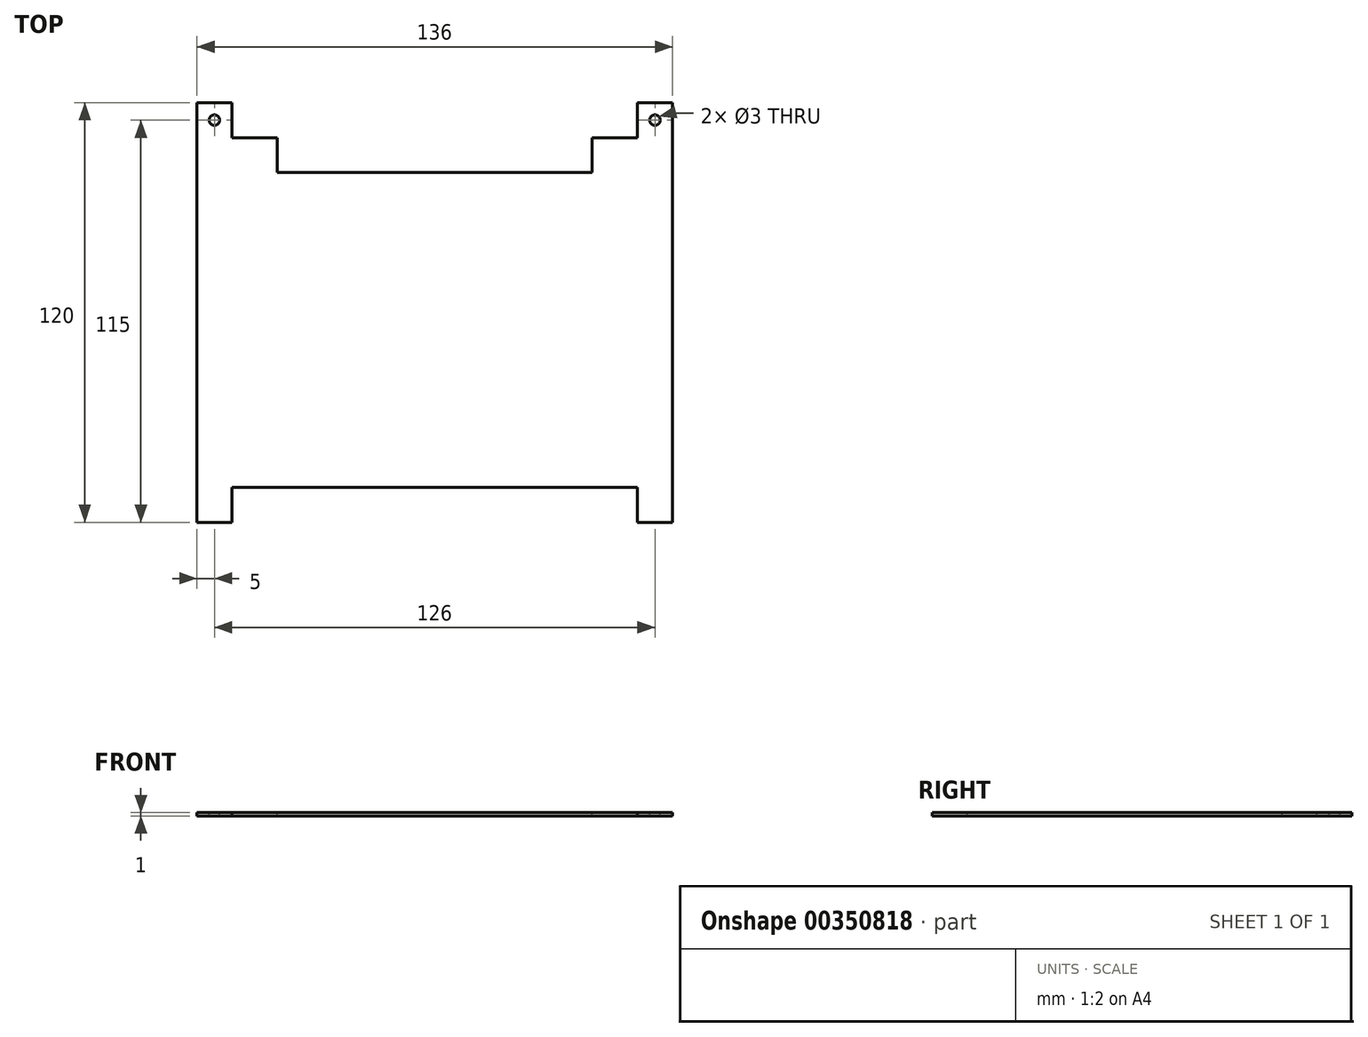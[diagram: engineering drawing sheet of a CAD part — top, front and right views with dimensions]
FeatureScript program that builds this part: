
annotation { "Feature Type Name" : "Feature", "Feature Type Description" : "" }
export const myFeature = defineFeature(function(context is Context, id is Id, definition is map)
    precondition{}
    {
        {
            var Q0;
            Q0=qCreatedBy(makeId("Top.planeOp"),FACE);
            var sketch = newSketch(context, id + "F0", { "sketchPlane" : qUnion([Q0])});
            skLineSegment(sketch, "E0.bottom", {"start": v(-68, -60) * mm, "end": v(68, -60) * mm});
            skLineSegment(sketch, "E0.top", {"start": v(-68, 60) * mm, "end": v(68, 60) * mm});
            skLineSegment(sketch, "E0.left", {"start": v(-68, -60) * mm, "end": v(-68, 60) * mm});
            skLineSegment(sketch, "E0.right", {"start": v(68, -60) * mm, "end": v(68, 60) * mm});
            skLineSegment(sketch, "E1", {"start": v(-17.73, 0) * mm, "end": v(16.73, 0) * mm, "construction": true});
            skLineSegment(sketch, "E2", {"start": v(0, 27.92) * mm, "end": v(0, -15.73) * mm, "construction": true});
            skSolve(sketch);
        }
        {
            var Q0;
            Q0 = qSketchRegion(id + "F0", true);
            extrude(context, id + "F1", {"entities" : qUnion([Q0]), "depth" : 1 * mm});
        }
        {
            var Q0;
            Q0=makeQuery(id+"F1.opExtrude","CAP_FACE",FACE,{"disambiguationData":[OSD([sQuery(id+"F0.wireOp",EDGE,"E0.bottom"),sQuery(id+"F0.wireOp",EDGE,"E0.top"),sQuery(id+"F0.wireOp",EDGE,"E0.left"),sQuery(id+"F0.wireOp",EDGE,"E0.right")])],"isStart":false});
            var sketch = newSketch(context, id + "F2", { "sketchPlane" : qUnion([Q0])});
            skLineSegment(sketch, "E3", {"start": v(-58, 60) * mm, "end": v(-58, 50) * mm});
            skLineSegment(sketch, "E4", {"start": v(-58, 50) * mm, "end": v(-45, 50) * mm});
            skLineSegment(sketch, "E5", {"start": v(-45, 50) * mm, "end": v(-45, 40) * mm});
            skLineSegment(sketch, "E6", {"start": v(-45, 40) * mm, "end": v(0, 40) * mm});
            skLineSegment(sketch, "E7", {"start": v(0, -10.8) * mm, "end": v(0, 68.44) * mm, "construction": true});
            skPoint(sketch, "E7.endSnap0", {"position": v(0, 60) * mm});
            skLineSegment(sketch, "E8.MirrorCS", {"start": v(58, 50) * mm, "end": v(45, 50) * mm});
            skLineSegment(sketch, "E9.MirrorCS", {"start": v(58, 60) * mm, "end": v(58, 50) * mm});
            skLineSegment(sketch, "E10.MirrorCS", {"start": v(45, 40) * mm, "end": v(0, 40) * mm});
            skLineSegment(sketch, "E11.MirrorCS", {"start": v(45, 50) * mm, "end": v(45, 40) * mm});
            skLineSegment(sketch, "E12", {"start": v(-58, 60) * mm, "end": v(58, 60) * mm});
            skLineSegment(sketch, "E13.bottom", {"start": v(-58, -60) * mm, "end": v(58, -60) * mm});
            skLineSegment(sketch, "E13.top", {"start": v(-58, -50) * mm, "end": v(58, -50) * mm});
            skLineSegment(sketch, "E13.left", {"start": v(-58, -60) * mm, "end": v(-58, -50) * mm});
            skLineSegment(sketch, "E13.right", {"start": v(58, -60) * mm, "end": v(58, -50) * mm});
            skSolve(sketch);
        }
        {
            var Q0;
            Q0 = qSketchRegion(id + "F2", true);
            extrude(context, id + "F3", {"entities" : qUnion([Q0]), "operationType" : NewBodyOperationType.REMOVE, "endBound" : BoundingType.UP_TO_NEXT, "oppositeDirection" : true, "depth" : 25 * mm});
        }
        {
            var Q0;
            Q0=makeQuery(id+"F1.opExtrude","CAP_FACE",FACE,{"disambiguationData":[OSD([sQuery(id+"F0.wireOp",EDGE,"E0.bottom"),sQuery(id+"F0.wireOp",EDGE,"E0.top"),sQuery(id+"F0.wireOp",EDGE,"E0.left"),sQuery(id+"F0.wireOp",EDGE,"E0.right")])],"isStart":false});
            var sketch = newSketch(context, id + "F4", { "sketchPlane" : qUnion([Q0])});
            skCircle(sketch, "E14", {"center": v(-63, 55) * mm, "radius": 1.5 * mm});
            skCircle(sketch, "E15", {"center": v(63, 55) * mm, "radius": 1.5 * mm});
            skPoint(sketch, "E16", {"position": v(-63, 60) * mm});
            skPoint(sketch, "E17", {"position": v(-58, 55) * mm});
            skPoint(sketch, "E18", {"position": v(58, 55) * mm});
            skPoint(sketch, "E19", {"position": v(63, 60) * mm});
            skSolve(sketch);
        }
        {
            var Q0;
            Q0 = qSketchRegion(id + "F4", true);
            extrude(context, id + "F5", {"entities" : qUnion([Q0]), "operationType" : NewBodyOperationType.REMOVE, "endBound" : BoundingType.UP_TO_NEXT, "oppositeDirection" : true, "depth" : 25 * mm});
        }
    });
